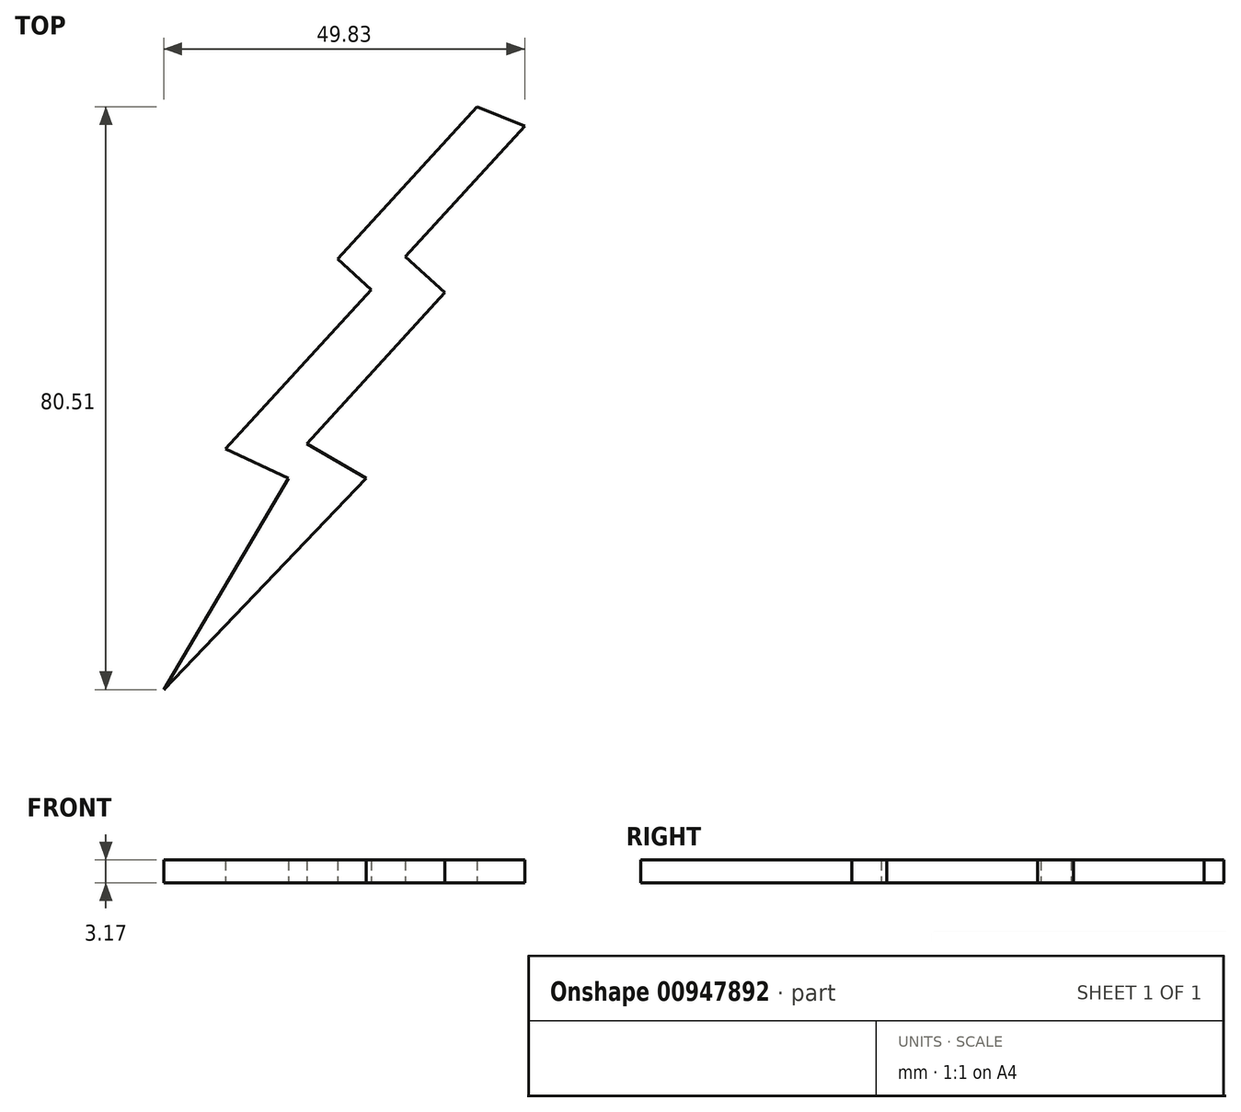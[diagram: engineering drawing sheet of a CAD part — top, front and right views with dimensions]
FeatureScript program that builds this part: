
annotation { "Feature Type Name" : "Feature", "Feature Type Description" : "" }
export const myFeature = defineFeature(function(context is Context, id is Id, definition is map)
    precondition{}
    {
        {
            var Q0;
            Q0=qCreatedBy(makeId("Top.planeOp"),FACE);
            var sketch = newSketch(context, id + "F0", { "sketchPlane" : qUnion([Q0])});
            skLineSegment(sketch, "E0", {"start": v(26.06, 51.33) * mm, "end": v(6.83, 30.3) * mm});
            skLineSegment(sketch, "E1", {"start": v(6.83, 30.3) * mm, "end": v(11.45, 26.08) * mm});
            skLineSegment(sketch, "E2", {"start": v(11.45, 26.08) * mm, "end": v(-8.68, 4.06) * mm});
            skLineSegment(sketch, "E3", {"start": v(-8.68, 4.06) * mm, "end": v(0, 0) * mm});
            skLineSegment(sketch, "E4", {"start": v(0, 0) * mm, "end": v(-17.2, -29.18) * mm});
            skLineSegment(sketch, "E5", {"start": v(-17.2, -29.18) * mm, "end": v(10.74, 0) * mm});
            skLineSegment(sketch, "E6", {"start": v(10.74, 0) * mm, "end": v(2.52, 4.81) * mm});
            skLineSegment(sketch, "E7", {"start": v(2.52, 4.81) * mm, "end": v(21.57, 25.65) * mm});
            skLineSegment(sketch, "E8", {"start": v(21.57, 25.65) * mm, "end": v(16.15, 30.6) * mm});
            skLineSegment(sketch, "E9", {"start": v(16.15, 30.6) * mm, "end": v(32.63, 48.63) * mm});
            skLineSegment(sketch, "E10", {"start": v(32.63, 48.63) * mm, "end": v(26.06, 51.33) * mm});
            skSolve(sketch);
        }
        {
            var Q0;
            Q0=makeQuery(id+"F0.imprint","IMPRINT",FACE,{"disambiguationData":[TD([[makeQuery(id+"F0.imprint","IMPRINT",EDGE,{"derivedFrom":sQuery(id+"F0.wireOp",EDGE,"E0")}),1.0]])]});
            extrude(context, id + "F1", {"entities" : qUnion([Q0]), "depth" : 3.17 * mm, "offsetDistance" : 25.4 * mm});
        }
    });
